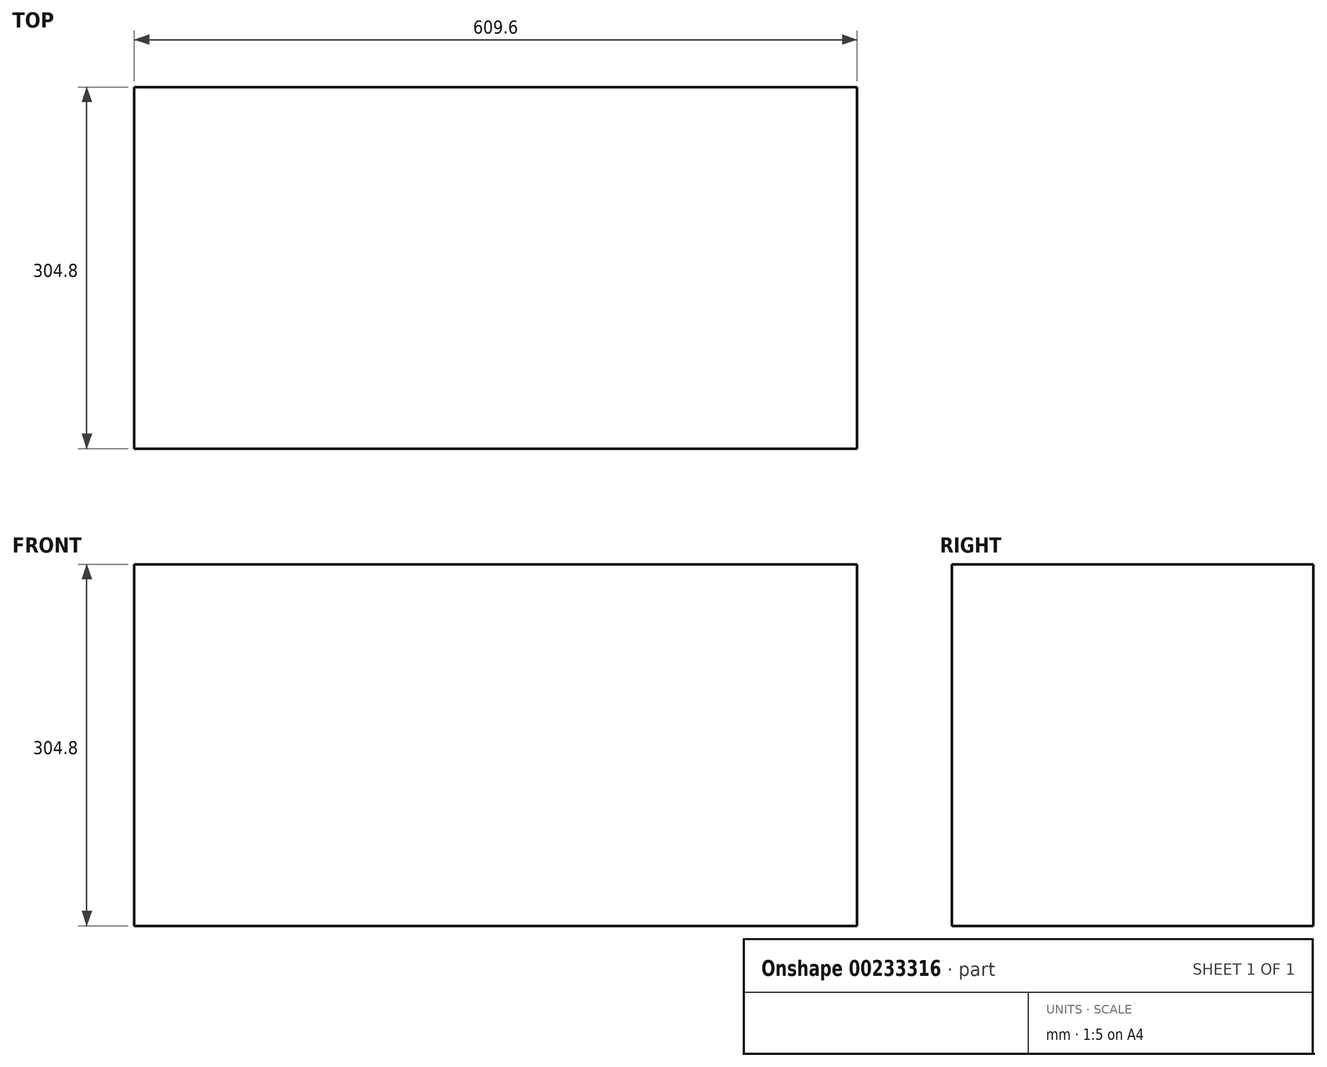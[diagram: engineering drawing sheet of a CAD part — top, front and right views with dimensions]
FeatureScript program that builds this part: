
annotation { "Feature Type Name" : "Feature", "Feature Type Description" : "" }
export const myFeature = defineFeature(function(context is Context, id is Id, definition is map)
    precondition{}
    {
        {
            var Q0;
            Q0=qCreatedBy(makeId("Top.planeOp"),FACE);
            var sketch = newSketch(context, id + "F0", { "sketchPlane" : qUnion([Q0])});
            skLineSegment(sketch, "E0.bottom", {"start": v(324.54, -152.4) * mm, "end": v(-285.06, -152.4) * mm});
            skLineSegment(sketch, "E0.top", {"start": v(324.54, 152.4) * mm, "end": v(-285.06, 152.4) * mm});
            skLineSegment(sketch, "E0.left", {"start": v(324.54, -152.4) * mm, "end": v(324.54, 152.4) * mm});
            skLineSegment(sketch, "E0.right", {"start": v(-285.06, -152.4) * mm, "end": v(-285.06, 152.4) * mm});
            skPoint(sketch, "E0.middle", {"position": v(19.74, 0) * mm});
            skSolve(sketch);
        }
        {
            var Q0;
            Q0=makeQuery(id+"F0.imprint","IMPRINT",FACE,{"disambiguationData":[TD([[makeQuery(id+"F0.imprint","IMPRINT",EDGE,{"derivedFrom":sQuery(id+"F0.wireOp",EDGE,"E0.bottom")}),-1.0]])]});
            extrude(context, id + "F1", {"entities" : qUnion([Q0]), "depth" : 304.8 * mm});
        }
    });
